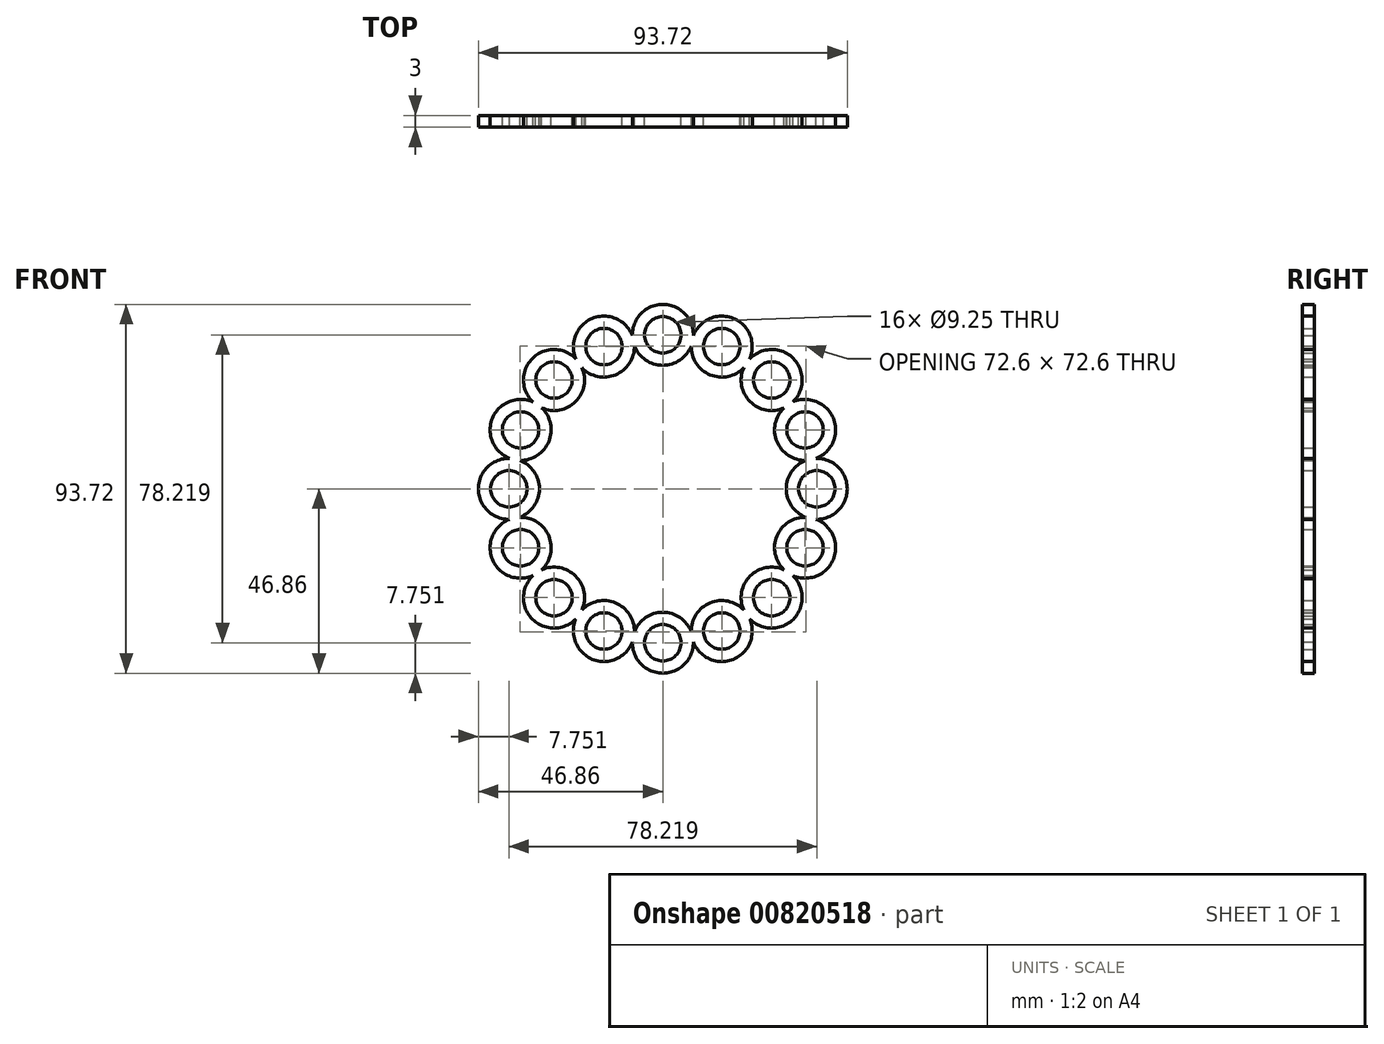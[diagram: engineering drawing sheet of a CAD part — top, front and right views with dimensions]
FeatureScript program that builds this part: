
annotation { "Feature Type Name" : "Feature", "Feature Type Description" : "" }
export const myFeature = defineFeature(function(context is Context, id is Id, definition is map)
    precondition{}
    {
        {
            var Q0;
            Q0=qCreatedBy(makeId("Front.planeOp"),FACE);
            var sketch = newSketch(context, id + "F0", { "sketchPlane" : qUnion([Q0])});
            skCircle(sketch, "E0", {"center": v(0, 39.1) * mm, "radius": 4.63 * mm});
            skArc(sketch, "E1", {"start": v(-7.22, 36.3) * mm, "mid": v(0, 31.36) * mm, "end": v(7.22, 36.3) * mm});
            skArc(sketch, "E2.trimOffspring", {"start": v(7.75, 38.94) * mm, "mid": v(0, 46.86) * mm, "end": v(-7.75, 38.94) * mm});
            skPoint(sketch, "E3.center", {"position": v(0, 0) * mm});
            skCircle(sketch, "E4.1.0", {"center": v(-14.97, 36.13) * mm, "radius": 4.63 * mm});
            skArc(sketch, "E4.1.1", {"start": v(-20.56, 30.78) * mm, "mid": v(-12, 28.97) * mm, "end": v(-7.22, 36.3) * mm});
            skArc(sketch, "E4.1.2", {"start": v(-7.75, 38.94) * mm, "mid": v(-17.93, 43.3) * mm, "end": v(-22.06, 33.01) * mm});
            skCircle(sketch, "E4.2.0", {"center": v(-27.65, 27.65) * mm, "radius": 4.63 * mm});
            skArc(sketch, "E4.2.1", {"start": v(-30.78, 20.56) * mm, "mid": v(-22.18, 22.18) * mm, "end": v(-20.56, 30.78) * mm});
            skArc(sketch, "E4.2.2", {"start": v(-22.06, 33.01) * mm, "mid": v(-33.13, 33.13) * mm, "end": v(-33.01, 22.06) * mm});
            skCircle(sketch, "E4.3.0", {"center": v(-36.13, 14.97) * mm, "radius": 4.63 * mm});
            skArc(sketch, "E4.3.1", {"start": v(-36.3, 7.22) * mm, "mid": v(-28.97, 12) * mm, "end": v(-30.78, 20.56) * mm});
            skArc(sketch, "E4.3.2", {"start": v(-33.01, 22.06) * mm, "mid": v(-43.3, 17.93) * mm, "end": v(-38.94, 7.75) * mm});
            skCircle(sketch, "E4.4.0", {"center": v(-39.1, 0) * mm, "radius": 4.63 * mm});
            skArc(sketch, "E4.4.1", {"start": v(-36.3, -7.22) * mm, "mid": v(-31.36, 0) * mm, "end": v(-36.3, 7.22) * mm});
            skArc(sketch, "E4.4.2", {"start": v(-38.94, 7.75) * mm, "mid": v(-46.86, 0) * mm, "end": v(-38.94, -7.75) * mm});
            skCircle(sketch, "E4.5.0", {"center": v(-36.13, -14.97) * mm, "radius": 4.63 * mm});
            skArc(sketch, "E4.5.1", {"start": v(-30.78, -20.56) * mm, "mid": v(-28.97, -12) * mm, "end": v(-36.3, -7.22) * mm});
            skArc(sketch, "E4.5.2", {"start": v(-38.94, -7.75) * mm, "mid": v(-43.3, -17.93) * mm, "end": v(-33.01, -22.06) * mm});
            skCircle(sketch, "E4.6.0", {"center": v(-27.65, -27.65) * mm, "radius": 4.63 * mm});
            skArc(sketch, "E4.6.1", {"start": v(-20.56, -30.78) * mm, "mid": v(-22.18, -22.18) * mm, "end": v(-30.78, -20.56) * mm});
            skArc(sketch, "E4.6.2", {"start": v(-33.01, -22.06) * mm, "mid": v(-33.13, -33.13) * mm, "end": v(-22.06, -33.01) * mm});
            skCircle(sketch, "E4.7.0", {"center": v(-14.97, -36.13) * mm, "radius": 4.63 * mm});
            skArc(sketch, "E4.7.1", {"start": v(-7.22, -36.3) * mm, "mid": v(-12, -28.97) * mm, "end": v(-20.56, -30.78) * mm});
            skArc(sketch, "E4.7.2", {"start": v(-22.06, -33.01) * mm, "mid": v(-17.93, -43.3) * mm, "end": v(-7.75, -38.94) * mm});
            skCircle(sketch, "E4.8.0", {"center": v(0, -39.1) * mm, "radius": 4.63 * mm});
            skArc(sketch, "E4.8.1", {"start": v(7.22, -36.3) * mm, "mid": v(0, -31.36) * mm, "end": v(-7.22, -36.3) * mm});
            skArc(sketch, "E4.8.2", {"start": v(-7.75, -38.94) * mm, "mid": v(0, -46.86) * mm, "end": v(7.75, -38.94) * mm});
            skCircle(sketch, "E4.9.0", {"center": v(14.97, -36.13) * mm, "radius": 4.63 * mm});
            skArc(sketch, "E4.9.1", {"start": v(20.56, -30.78) * mm, "mid": v(12, -28.97) * mm, "end": v(7.22, -36.3) * mm});
            skArc(sketch, "E4.9.2", {"start": v(7.75, -38.94) * mm, "mid": v(17.93, -43.3) * mm, "end": v(22.06, -33.01) * mm});
            skCircle(sketch, "E4.10.0", {"center": v(27.65, -27.65) * mm, "radius": 4.63 * mm});
            skArc(sketch, "E4.10.1", {"start": v(30.78, -20.56) * mm, "mid": v(22.18, -22.18) * mm, "end": v(20.56, -30.78) * mm});
            skArc(sketch, "E4.10.2", {"start": v(22.06, -33.01) * mm, "mid": v(33.13, -33.13) * mm, "end": v(33.01, -22.06) * mm});
            skCircle(sketch, "E4.11.0", {"center": v(36.13, -14.97) * mm, "radius": 4.63 * mm});
            skArc(sketch, "E4.11.1", {"start": v(36.3, -7.22) * mm, "mid": v(28.97, -12) * mm, "end": v(30.78, -20.56) * mm});
            skArc(sketch, "E4.11.2", {"start": v(33.01, -22.06) * mm, "mid": v(43.3, -17.93) * mm, "end": v(38.94, -7.75) * mm});
            skCircle(sketch, "E4.12.0", {"center": v(39.1, 0) * mm, "radius": 4.63 * mm});
            skArc(sketch, "E4.12.1", {"start": v(36.3, 7.22) * mm, "mid": v(31.36, 0) * mm, "end": v(36.3, -7.22) * mm});
            skArc(sketch, "E4.12.2", {"start": v(38.94, -7.75) * mm, "mid": v(46.86, 0) * mm, "end": v(38.94, 7.75) * mm});
            skCircle(sketch, "E4.13.0", {"center": v(36.13, 14.97) * mm, "radius": 4.63 * mm});
            skArc(sketch, "E4.13.1", {"start": v(30.78, 20.56) * mm, "mid": v(28.97, 12) * mm, "end": v(36.3, 7.22) * mm});
            skArc(sketch, "E4.13.2", {"start": v(38.94, 7.75) * mm, "mid": v(43.3, 17.93) * mm, "end": v(33.01, 22.06) * mm});
            skCircle(sketch, "E4.14.0", {"center": v(27.65, 27.65) * mm, "radius": 4.63 * mm});
            skArc(sketch, "E4.14.1", {"start": v(20.56, 30.78) * mm, "mid": v(22.18, 22.18) * mm, "end": v(30.78, 20.56) * mm});
            skArc(sketch, "E4.14.2", {"start": v(33.01, 22.06) * mm, "mid": v(33.13, 33.13) * mm, "end": v(22.06, 33.01) * mm});
            skCircle(sketch, "E4.15.0", {"center": v(14.97, 36.13) * mm, "radius": 4.63 * mm});
            skArc(sketch, "E4.15.1", {"start": v(7.22, 36.3) * mm, "mid": v(12, 28.97) * mm, "end": v(20.56, 30.78) * mm});
            skArc(sketch, "E4.15.2", {"start": v(22.06, 33.01) * mm, "mid": v(17.93, 43.3) * mm, "end": v(7.75, 38.94) * mm});
            skCircle(sketch, "E5", {"center": v(0, 0) * mm, "radius": 11 * mm});
            skSolve(sketch);
        }
        {
            var Q0;
            Q0 = qSketchRegion(id + "F0", true);
            extrude(context, id + "F1", {"entities" : qUnion([Q0]), "depth" : 3 * mm, "offsetDistance" : 25 * mm});
        }
    });
